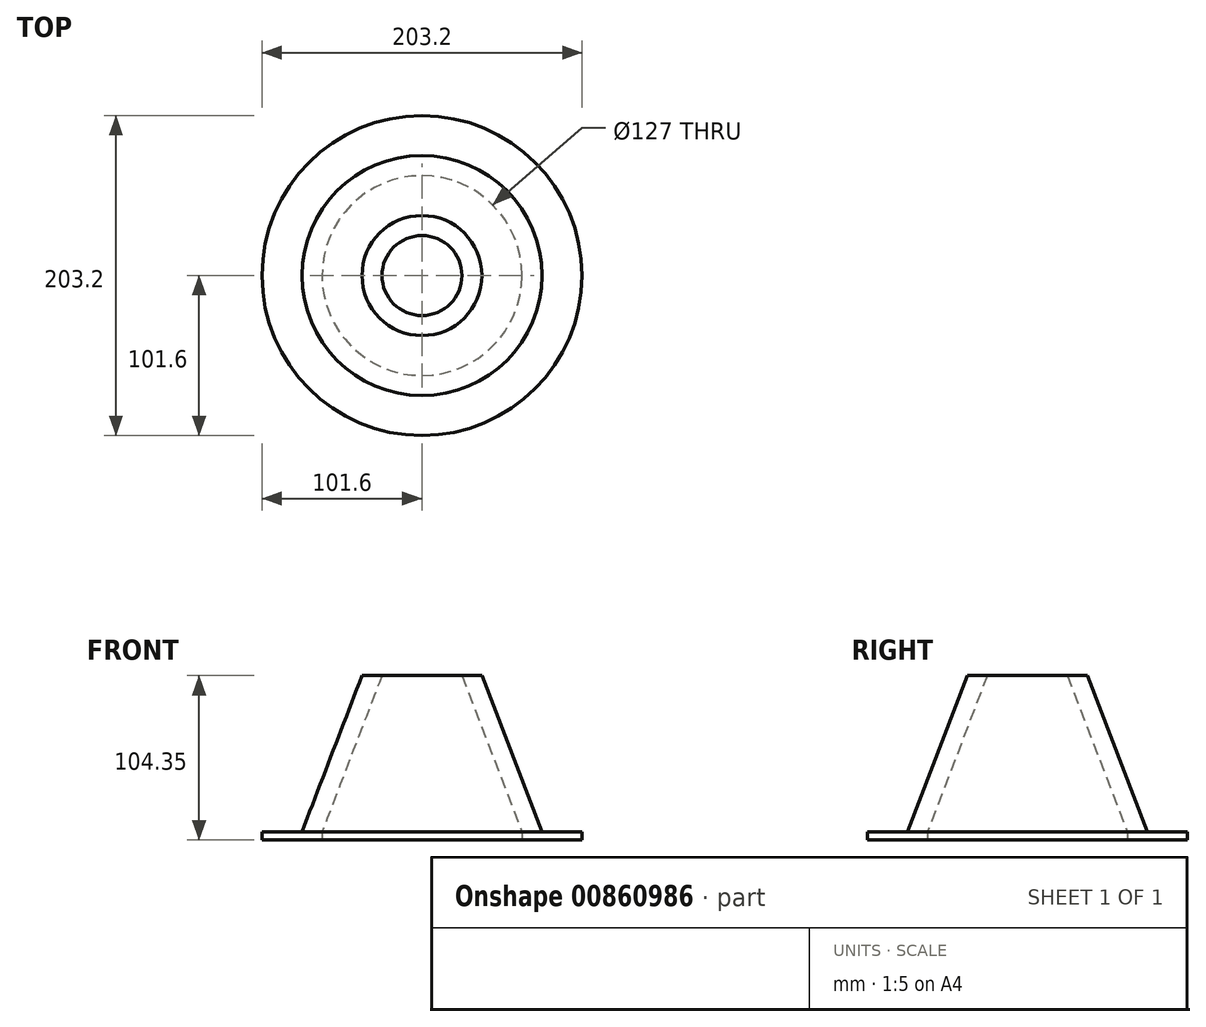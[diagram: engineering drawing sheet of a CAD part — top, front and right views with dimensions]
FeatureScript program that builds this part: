
annotation { "Feature Type Name" : "Feature", "Feature Type Description" : "" }
export const myFeature = defineFeature(function(context is Context, id is Id, definition is map)
    precondition{}
    {
        {
            var Q0;
            Q0=qCreatedBy(makeId("Front.planeOp"),FACE);
            var sketch = newSketch(context, id + "F0", { "sketchPlane" : qUnion([Q0])});
            skLineSegment(sketch, "E0", {"start": v(101.6, 0) * mm, "end": v(101.6, 5.08) * mm});
            skLineSegment(sketch, "E1", {"start": v(101.6, 5.08) * mm, "end": v(76.2, 5.08) * mm});
            skLineSegment(sketch, "E2", {"start": v(76.2, 5.08) * mm, "end": v(38.1, 104.35) * mm});
            skLineSegment(sketch, "E3", {"start": v(38.1, 104.35) * mm, "end": v(25.4, 104.35) * mm});
            skLineSegment(sketch, "E4", {"start": v(25.4, 104.35) * mm, "end": v(63.5, 5.08) * mm});
            skLineSegment(sketch, "E5", {"start": v(63.5, 5.08) * mm, "end": v(63.5, 0) * mm});
            skLineSegment(sketch, "E6", {"start": v(63.5, 0) * mm, "end": v(101.6, 0) * mm});
            skLineSegment(sketch, "E7", {"start": v(0, -31.07) * mm, "end": v(0, 137.47) * mm, "construction": true});
            skSolve(sketch);
        }
        {
            var Q0;
            Q0=makeQuery(id+"F0.imprint","IMPRINT",FACE,{"disambiguationData":[TD([[makeQuery(id+"F0.imprint","IMPRINT",EDGE,{"derivedFrom":sQuery(id+"F0.wireOp",EDGE,"E0")}),1.0]])]});
            var Q1;
            Q1=sQuery(id+"F0.wireOp",EDGE,"E7");
            revolve(context, id + "F1", {"surfaceOperationType" : NewSurfaceOperationType.NEW, "entities" : qUnion([Q0]), "axis" : qUnion([Q1]), "revolveType" : RevolveType.FULL});
        }
    });
